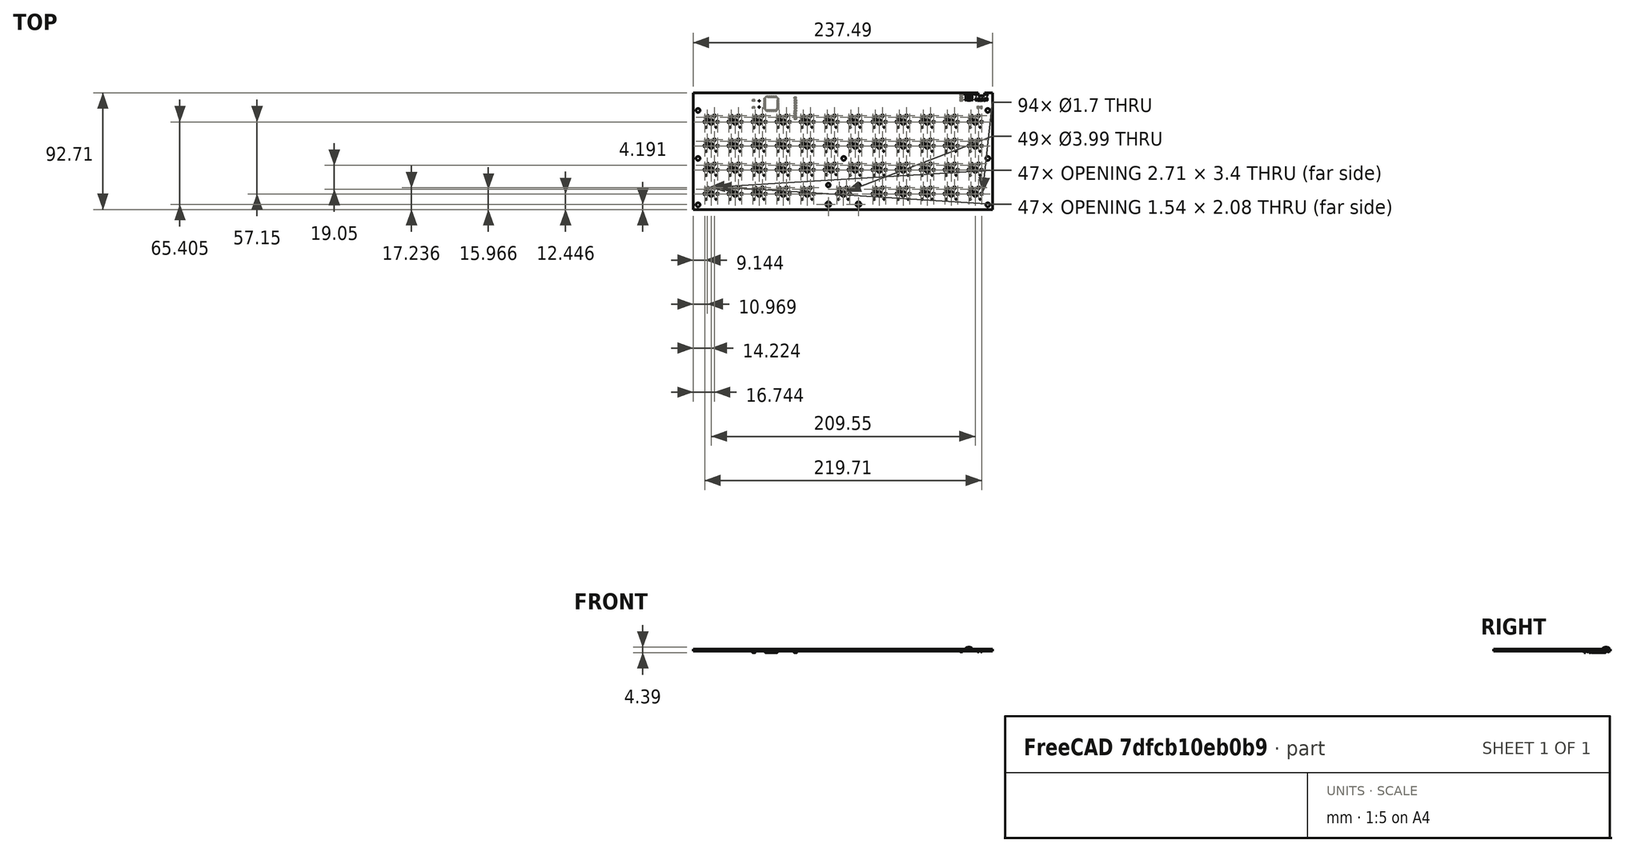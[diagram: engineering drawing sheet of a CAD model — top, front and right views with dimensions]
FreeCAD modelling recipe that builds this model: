
FCSTD DOCUMENT  (FreeCAD 0.18R4 (GitTag))
Label: Model2_Case
License: All rights reserved
LicenseURL: http://en.wikipedia.org/wiki/All_rights_reserved
objects: Part::Feature×19, Part::Part2DObjectPython×19, PartDesign::Body×11, App::Part×5, Sketcher::SketchObject×2, PartDesign::CoordinateSystem×1
note: 52 computed .brp shape members not serialized (recipe doc carries the construction recipe); baked Part::Feature solids carry a one-line shape summary decoded from their .brp

FEATURE [PartDesign::CoordinateSystem] Local_CS_5d60
  AttacherType = Attacher::AttachEngine3D
FEATURE [Sketcher::SketchObject] PCB_Sketch_5d60
  sketch-geometry (8):
    g0: LineSegment StartX=161.29 StartY=10.414 StartZ=0 EndX=161.29 EndY=12.7 EndZ=0
    g1: LineSegment StartX=156.21 StartY=12.7 StartZ=0 EndX=156.21 EndY=10.414 EndZ=0
    g2: LineSegment StartX=156.21 StartY=10.414 StartZ=0 EndX=161.29 EndY=10.414 EndZ=0
    g3: LineSegment StartX=-69.85 StartY=12.7 StartZ=0 EndX=-69.85 EndY=-80.01 EndZ=0
    g4: LineSegment StartX=156.21 StartY=12.7 StartZ=0 EndX=-69.85 EndY=12.7 EndZ=0
    g5: LineSegment StartX=167.64 StartY=12.7 StartZ=0 EndX=161.29 EndY=12.7 EndZ=0
    g6: LineSegment StartX=167.64 StartY=-80.01 StartZ=0 EndX=167.64 EndY=12.7 EndZ=0
    g7: LineSegment StartX=-69.85 StartY=-80.01 StartZ=0 EndX=167.64 EndY=-80.01 EndZ=0
  constraints (14):
    c: Coincident(g3,g7)
    c: Coincident(g3,g4)
    c: Coincident(g1,g2)
    c: Coincident(g1,g4)
    c: Coincident(g0,g2)
    c: Coincident(g0,g5)
    c: Coincident(g6,g7)
    c: Coincident(g5,g6)
    c: DistanceY(g3,g3) = 92.71
    c: DistanceX(g3,g6) = 237.49
    c: Parallel(g7,g4)
    c: Parallel(g4,g2)
    c: Parallel(g2,g5)
    c: Parallel(g1,g0)
FEATURE [Part::Feature] Shape  label="D48_LED_0805_2012Metric_5F689551"
  Placement = pos=(11.176,-7.62,-1.6) rot=(1,0,0;3.14159rad)
  shape: bbox 2 x 1.25 x 1.1 mm, 50 faces (baked)
FEATURE [Part::Feature] Shape001  label="R7_R_0805_2012Metric_5F6845C1"
  Placement = pos=(11.176,-5.588,-1.6) rot=(0,1,0;3.14159rad)
  shape: bbox 2 x 1.2 x 0.45 mm, 26 faces (baked)
FEATURE [Part::Feature] Shape002  label="U1_TQFP_44_10x10mm_P08mm_5F58FB19"
  Placement = pos=(-7.874,4.064,-1.6) rot=(0.707107,0.707107,0;3.14159rad)
  shape: bbox 12 x 12 x 1.1 mm, 704 faces (baked)
FEATURE [Part::Feature] Shape003  label="C3_C_0805_2012Metric_5F58EEA5"
  Placement = pos=(11.176,6.604,-1.6) rot=(1,0,0;3.14159rad)
  shape: bbox 2 x 1.25 x 1.25 mm, 28 faces (baked)
FEATURE [Part::Feature] Shape004  label="C1_C_0805_2012Metric_5F58EE83"
  Placement = pos=(-21.844,6.604,-1.6) rot=(0,1,0;3.14159rad)
  shape: bbox 2 x 1.25 x 1.25 mm, 28 faces (baked)
FEATURE [Part::Feature] Shape005  label="C2_C_0805_2012Metric_5F58EE94"
  Placement = pos=(-21.844,1.016,-1.6) rot=(0,1,0;3.14159rad)
  shape: bbox 2 x 1.25 x 1.25 mm, 28 faces (baked)
FEATURE [Part::Feature] Shape006  label="C4_C_0805_2012Metric_5F58EEB6"
  Placement = pos=(11.176,4.572,-1.6) rot=(1,0,0;3.14159rad)
  shape: bbox 2 x 1.25 x 1.25 mm, 28 faces (baked)
FEATURE [Part::Feature] Shape007  label="C5_C_0805_2012Metric_5F58EEC7"
  Placement = pos=(11.176,2.54,-1.6) rot=(1,0,0;3.14159rad)
  shape: bbox 2 x 1.25 x 1.25 mm, 28 faces (baked)
FEATURE [Part::Feature] Shape008  label="C6_C_0805_2012Metric_5F58EED8"
  Placement = pos=(11.176,0.508,-1.6) rot=(1,0,0;3.14159rad)
  shape: bbox 2 x 1.25 x 1.25 mm, 28 faces (baked)
FEATURE [Part::Feature] Shape009  label="C7_C_0805_2012Metric_5F58EEE9"
  Placement = pos=(11.176,-1.524,-1.6) rot=(1,0,0;3.14159rad)
  shape: bbox 2 x 1.25 x 1.25 mm, 28 faces (baked)
FEATURE [Part::Feature] Shape010  label="C8_C_0805_2012Metric_5F58EEFA"
  Placement = pos=(11.176,-3.556,-1.6) rot=(0,1,0;3.14159rad)
  shape: bbox 2 x 1.25 x 1.25 mm, 28 faces (baked)
FEATURE [Part::Feature] Shape011  label="R1_R_0805_2012Metric_5F58F99D"
  Placement = pos=(142.748,6.858,-1.6) rot=(1,0,0;3.14159rad)
  shape: bbox 2 x 1.2 x 0.45 mm, 26 faces (baked)
FEATURE [Part::Feature] Shape012  label="R2_R_0805_2012Metric_5F58F9AE"
  Placement = pos=(11.176,8.636,-1.6) rot=(0,1,0;3.14159rad)
  shape: bbox 2 x 1.2 x 0.45 mm, 26 faces (baked)
FEATURE [Part::Feature] Shape013  label="R3_R_0805_2012Metric_5F59C62D"
  Placement = pos=(142.748,8.89,-1.6) rot=(1,0,0;3.14159rad)
  shape: bbox 2 x 1.2 x 0.45 mm, 26 faces (baked)
FEATURE [Part::Feature] Shape014  label="R4_R_0805_2012Metric_5F58F9D0"
  Placement = pos=(142.748,10.922,-1.6) rot=(1,0,0;3.14159rad)
  shape: bbox 2 x 1.2 x 0.45 mm, 26 faces (baked)
FEATURE [Part::Feature] Shape015  label="SW1_SW_SPST_TL3342_5F58FA06"
  Placement = pos=(148.844,9.144,0) rot=(0,0,1;0rad)
  shape: bbox 6.401 x 5.201 x 1.541 mm, 193 faces (baked)
FEATURE [App::Part] Top_5d60
  Group = -> [Shape015]
  Origin = -> Origin003
FEATURE [Part::Feature] Shape016  label="R5_R_0805_2012Metric_5F678B00"
  Placement = pos=(158.75,1.27,-1.6) rot=(0.707107,0.707107,0;3.14159rad)
  shape: bbox 1.2 x 2 x 0.45 mm, 26 faces (baked)
FEATURE [Part::Feature] Shape017  label="R6_R_0805_2012Metric_5F6787FB"
  Placement = pos=(156.21,1.27,-1.6) rot=(0.707107,0.707107,0;3.14159rad)
  shape: bbox 1.2 x 2 x 0.45 mm, 26 faces (baked)
FEATURE [App::Part] Bot_5d60
  Group = -> [Shape,Shape001,Shape002,Shape003,Shape004,Shape005,Shape006,Shape007,Shape008,Shape009,Shape010,Shape011,Shape012,Shape013,Shape014,Shape016,Shape017]
  Origin = -> Origin004
FEATURE [App::Part] Step_Models_5d60
  Group = -> [Top_5d60,Bot_5d60]
  Origin = -> Origin002
FEATURE [Part::Feature] Pcb_5d60
  Placement = pos=(-85.344,47.244,0) rot=(0,0,1;0rad)
  shape: bbox 237.5 x 92.71 x 1.6 mm, 862 faces (baked)
FEATURE [Part::Part2DObjectPython] Line  label="bl_left"  # Draft 2D object (typed FeaturePython)
  ChamferSize = 0
  Closed = false
  End = (-69.85,-76.2,0)
  FilletRadius = 0
  Length = 3.81
  MakeFace = false
  Placement = pos=(-66.04,-76.2,0) rot=(0,0,1;0rad)
  Points = (2) [(0,0,0),(-3.81,-1.42109e-14,0)]
  Start = (-66.04,-76.2,0)
  Subdivisions = 0
FEATURE [Part::Part2DObjectPython] Line003  label="bl_down"  # Draft 2D object (typed FeaturePython)
  ChamferSize = 0
  Closed = false
  End = (-66.04,-80.01,0)
  FilletRadius = 0
  Length = 3.81
  MakeFace = false
  Placement = pos=(-66.04,-76.2,0) rot=(0,0,1;0rad)
  Points = (2) [(0,0,0),(0,-3.81,0)]
  Start = (-66.04,-76.2,0)
  Subdivisions = 0
FEATURE [Part::Part2DObjectPython] Line004  label="ml_bl"  # Draft 2D object (typed FeaturePython)
  ChamferSize = 0
  Closed = false
  End = (-66.04,-39.37,0)
  FilletRadius = 0
  Length = 36.83
  MakeFace = false
  Placement = pos=(-66.04,-76.2,0) rot=(0,0,1;0rad)
  Points = (2) [(0,0,0),(0,36.83,0)]
  Start = (-66.04,-76.2,0)
  Subdivisions = 0
FEATURE [Part::Part2DObjectPython] Line005  label="ml_left"  # Draft 2D object (typed FeaturePython)
  ChamferSize = 0
  Closed = false
  End = (-69.85,-39.37,0)
  FilletRadius = 0
  Length = 3.81
  MakeFace = false
  Placement = pos=(-66.04,-39.37,0) rot=(0,0,1;0rad)
  Points = (2) [(0,0,0),(-3.81,0,0)]
  Start = (-66.04,-39.37,0)
  Subdivisions = 0
FEATURE [Part::Part2DObjectPython] Line007  label="tl_left"  # Draft 2D object (typed FeaturePython)
  ChamferSize = 0
  Closed = false
  End = (-69.85,-1.27,0)
  FilletRadius = 0
  Length = 3.81
  MakeFace = false
  Placement = pos=(-66.04,-1.27,0) rot=(0,0,1;0rad)
  Points = (2) [(0,0,0),(-3.81,2.22045e-16,0)]
  Start = (-66.04,-1.27,0)
  Subdivisions = 0
FEATURE [Part::Part2DObjectPython] Line008  label="tl_ml"  # Draft 2D object (typed FeaturePython)
  ChamferSize = 0
  Closed = false
  End = (-66.04,-1.27,0)
  FilletRadius = 0
  Length = 38.1
  MakeFace = false
  Placement = pos=(-66.04,-39.37,0) rot=(0,0,1;0rad)
  Points = (2) [(0,0,0),(0,38.1,0)]
  Start = (-66.04,-39.37,0)
  Subdivisions = 0
FEATURE [Part::Part2DObjectPython] Line009  label="tl_tr"  # Draft 2D object (typed FeaturePython)
  ChamferSize = 0
  Closed = false
  End = (163.83,-1.27,0)
  FilletRadius = 0
  Length = 229.87
  MakeFace = false
  Placement = pos=(-66.04,-1.27,0) rot=(0,0,1;0rad)
  Points = (2) [(0,0,0),(229.87,-7.10543e-15,0)]
  Start = (-66.04,-1.27,0)
  Subdivisions = 0
FEATURE [Part::Part2DObjectPython] Line010  label="ml_mr"  # Draft 2D object (typed FeaturePython)
  ChamferSize = 0
  Closed = false
  End = (163.83,-39.37,0)
  FilletRadius = 0
  Length = 229.87
  MakeFace = false
  Placement = pos=(-66.04,-39.37,0) rot=(0,0,1;0rad)
  Points = (2) [(0,0,0),(229.87,-7.10543e-15,0)]
  Start = (-66.04,-39.37,0)
  Subdivisions = 0
FEATURE [Part::Part2DObjectPython] Line011  label="bl_br"  # Draft 2D object (typed FeaturePython)
  ChamferSize = 0
  Closed = false
  End = (163.83,-76.2,0)
  FilletRadius = 0
  Length = 229.87
  MakeFace = false
  Placement = pos=(-66.04,-76.2,0) rot=(0,0,1;0rad)
  Points = (2) [(0,0,0),(229.87,0,0)]
  Start = (-66.04,-76.2,0)
  Subdivisions = 0
FEATURE [Part::Part2DObjectPython] Line012  label="tl_up"  # Draft 2D object (typed FeaturePython)
  ChamferSize = 0
  Closed = false
  End = (-66.04,12.7,0)
  FilletRadius = 0
  Length = 13.97
  MakeFace = false
  Placement = pos=(-66.04,-1.27,0) rot=(0,0,1;0rad)
  Points = (2) [(0,0,0),(0,13.97,0)]
  Start = (-66.04,-1.27,0)
  Subdivisions = 0
FEATURE [Part::Part2DObjectPython] Line013  label="tr_up"  # Draft 2D object (typed FeaturePython)
  ChamferSize = 0
  Closed = false
  End = (163.83,12.7,0)
  FilletRadius = 0
  Length = 13.97
  MakeFace = false
  Placement = pos=(163.83,-1.27,0) rot=(0,0,1;0rad)
  Points = (2) [(0,0,0),(0,13.97,0)]
  Start = (163.83,-1.27,0)
  Subdivisions = 0
FEATURE [Part::Part2DObjectPython] Line014  label="tr_right"  # Draft 2D object (typed FeaturePython)
  ChamferSize = 0
  Closed = false
  End = (167.64,-1.27,0)
  FilletRadius = 0
  Length = 3.81
  MakeFace = false
  Placement = pos=(163.83,-1.27,0) rot=(0,0,1;0rad)
  Points = (2) [(0,0,0),(3.81,7.10543e-15,0)]
  Start = (163.83,-1.27,0)
  Subdivisions = 0
FEATURE [Part::Part2DObjectPython] Line015  label="tr_mr"  # Draft 2D object (typed FeaturePython)
  ChamferSize = 0
  Closed = false
  End = (163.83,-39.37,0)
  FilletRadius = 0
  Length = 38.1
  MakeFace = false
  Placement = pos=(163.83,-1.27,0) rot=(0,0,1;0rad)
  Points = (2) [(0,0,0),(0,-38.1,0)]
  Start = (163.83,-1.27,0)
  Subdivisions = 0
FEATURE [Part::Part2DObjectPython] Line016  label="mr_right"  # Draft 2D object (typed FeaturePython)
  ChamferSize = 0
  Closed = false
  End = (167.64,-39.37,0)
  FilletRadius = 0
  Length = 3.81
  MakeFace = false
  Placement = pos=(163.83,-39.37,0) rot=(0,0,1;0rad)
  Points = (2) [(0,0,0),(3.81,0,0)]
  Start = (163.83,-39.37,0)
  Subdivisions = 0
FEATURE [Part::Part2DObjectPython] Line017  label="mr_br"  # Draft 2D object (typed FeaturePython)
  ChamferSize = 0
  Closed = false
  End = (163.83,-76.2,0)
  FilletRadius = 0
  Length = 36.83
  MakeFace = false
  Placement = pos=(163.83,-39.37,0) rot=(0,0,1;0rad)
  Points = (2) [(0,0,0),(0,-36.83,0)]
  Start = (163.83,-39.37,0)
  Subdivisions = 0
FEATURE [Part::Part2DObjectPython] Line018  label="br_right"  # Draft 2D object (typed FeaturePython)
  ChamferSize = 0
  Closed = false
  End = (167.64,-76.2,0)
  FilletRadius = 0
  Length = 3.81
  MakeFace = false
  Placement = pos=(163.83,-76.2,0) rot=(0,0,1;0rad)
  Points = (2) [(0,0,0),(3.81,0,0)]
  Start = (163.83,-76.2,0)
  Subdivisions = 0
FEATURE [Part::Part2DObjectPython] Line019  label="br_down"  # Draft 2D object (typed FeaturePython)
  ChamferSize = 0
  Closed = false
  End = (163.83,-80.01,0)
  FilletRadius = 0
  Length = 3.81
  MakeFace = false
  Placement = pos=(163.83,-76.2,0) rot=(0,0,1;0rad)
  Points = (2) [(0,0,0),(0,-3.81,0)]
  Start = (163.83,-76.2,0)
  Subdivisions = 0
FEATURE [Part::Part2DObjectPython] Line020  label="width"  # Draft 2D object (typed FeaturePython)
  ChamferSize = 0
  Closed = false
  End = (167.64,-36.4771,0)
  FilletRadius = 0
  Length = 237.253
  MakeFace = false
  Placement = pos=(-69.6132,-36.4771,0) rot=(0,0,1;0rad)
  Points = (2) [(0,0,0),(237.253,-7.10543e-15,0)]
  Start = (-69.6132,-36.4771,0)
  Subdivisions = 0
FEATURE [Part::Part2DObjectPython] Line021  label="height"  # Draft 2D object (typed FeaturePython)
  ChamferSize = 0
  Closed = false
  End = (48.895,12.7,0)
  FilletRadius = 0
  Length = 92.71
  MakeFace = false
  Placement = pos=(48.895,-80.01,0) rot=(0,0,1;0rad)
  Points = (2) [(0,0,0),(0,92.71,0)]
  Start = (48.895,-80.01,0)
  Subdivisions = 0
FEATURE [PartDesign::Body] Body
  Origin = -> Origin005
FEATURE [PartDesign::Body] Body001
  Origin = -> Origin006
FEATURE [PartDesign::Body] Body002
  Origin = -> Origin007
FEATURE [PartDesign::Body] Body003
  Origin = -> Origin008
FEATURE [PartDesign::Body] Body004
  Origin = -> Origin009
FEATURE [PartDesign::Body] Body005
  Origin = -> Origin010
FEATURE [PartDesign::Body] Body006
  Origin = -> Origin011
FEATURE [PartDesign::Body] Body007
  Origin = -> Origin012
FEATURE [PartDesign::Body] Body008
  Origin = -> Origin013
FEATURE [PartDesign::Body] Body009
  Origin = -> Origin014
FEATURE [App::Part] Board_Geoms_5d60
  Group = -> [Local_CS_5d60,Pcb_5d60,PCB_Sketch_5d60,Body,Body001,Body002,Body003,Body004,Body005,Body006,Body007,Body008,Body009]
  Origin = -> Origin
FEATURE [App::Part] Board_5d60  label="rev4_plot"
  Group = -> [Board_Geoms_5d60,Step_Models_5d60]
  Origin = -> Origin001
FEATURE [Sketcher::SketchObject] Sketch  label="pcb_sketch"
  MapMode = 5
  Placement = pos=(0,0,3.4) rot=(1,0,0;3.14159rad)
  sketch-geometry (10):
    g0: LineSegment StartX=-118.625 StartY=-46.355 StartZ=0 EndX=118.625 EndY=-46.355 EndZ=0
    g1: LineSegment StartX=118.625 StartY=-46.355 StartZ=0 EndX=118.625 EndY=46.355 EndZ=0
    g2: LineSegment StartX=118.625 StartY=46.355 StartZ=0 EndX=-118.625 EndY=46.355 EndZ=0
    g3: LineSegment StartX=-118.625 StartY=46.355 StartZ=0 EndX=-118.625 EndY=-46.355 EndZ=0
    g4: Circle CenterX=-114.815 CenterY=-42.545 CenterZ=0 NormalX=0 NormalY=0 NormalZ=1 AngleXU=0 Radius=1.25
    g5: Circle CenterX=-114.815 CenterY=-5.715 CenterZ=0 NormalX=0 NormalY=0 NormalZ=1 AngleXU=0 Radius=1.25
    g6: Circle CenterX=-114.815 CenterY=32.385 CenterZ=0 NormalX=0 NormalY=0 NormalZ=1 AngleXU=0 Radius=1.25
    g7: Circle CenterX=114.815 CenterY=-42.545 CenterZ=0 NormalX=0 NormalY=0 NormalZ=1 AngleXU=0 Radius=1.25
    g8: Circle CenterX=114.815 CenterY=-5.715 CenterZ=0 NormalX=0 NormalY=0 NormalZ=1 AngleXU=0 Radius=1.25
    g9: Circle CenterX=114.815 CenterY=32.385 CenterZ=0 NormalX=0 NormalY=0 NormalZ=1 AngleXU=0 Radius=1.25
  constraints (29):
    c: Coincident(g0,g1)
    c: Coincident(g1,g2)
    c: Coincident(g3,g0)
    c: Horizontal(g0)
    c: Vertical(g3)
    c: DistanceX(g2,g1) = 237.25  'xLen'
    c: DistanceY(g0,g2) = 92.71  'yLen'
    c: Equal(g1,g3)
    c: Equal(g2,g0)
    c: Symmetric(g1,g2,g-2)
    c: Symmetric(g2,g0,g-1)
    c: Distance(g4,g3) = 3.81
    c: Distance(g5,g3) = 3.81
    c: Distance(g6,g3) = 3.81
    c: Distance(g4,g0) = 3.81
    c: Distance(g4,g5) = 36.83
    c: Distance(g5,g6) = 38.1
    c: Distance(g7,g1) = 3.81
    c: Distance(g7,g0) = 3.81
    c: Distance(g8,g1) = 3.81
    c: Distance(g7,g8) = 36.83
    c: Distance(g9,g1) = 3.81
    c: Distance(g8,g9) = 38.1
    c: Diameter(g9) = 2.5
    c: Equal(g9,g6)
    c: Equal(g9,g5)
    c: Equal(g9,g4)
    c: Equal(g9,g7)
    c: Equal(g9,g8)
FEATURE [PartDesign::Body] Body010
  Group = -> [Sketch]
  Origin = -> Origin015
